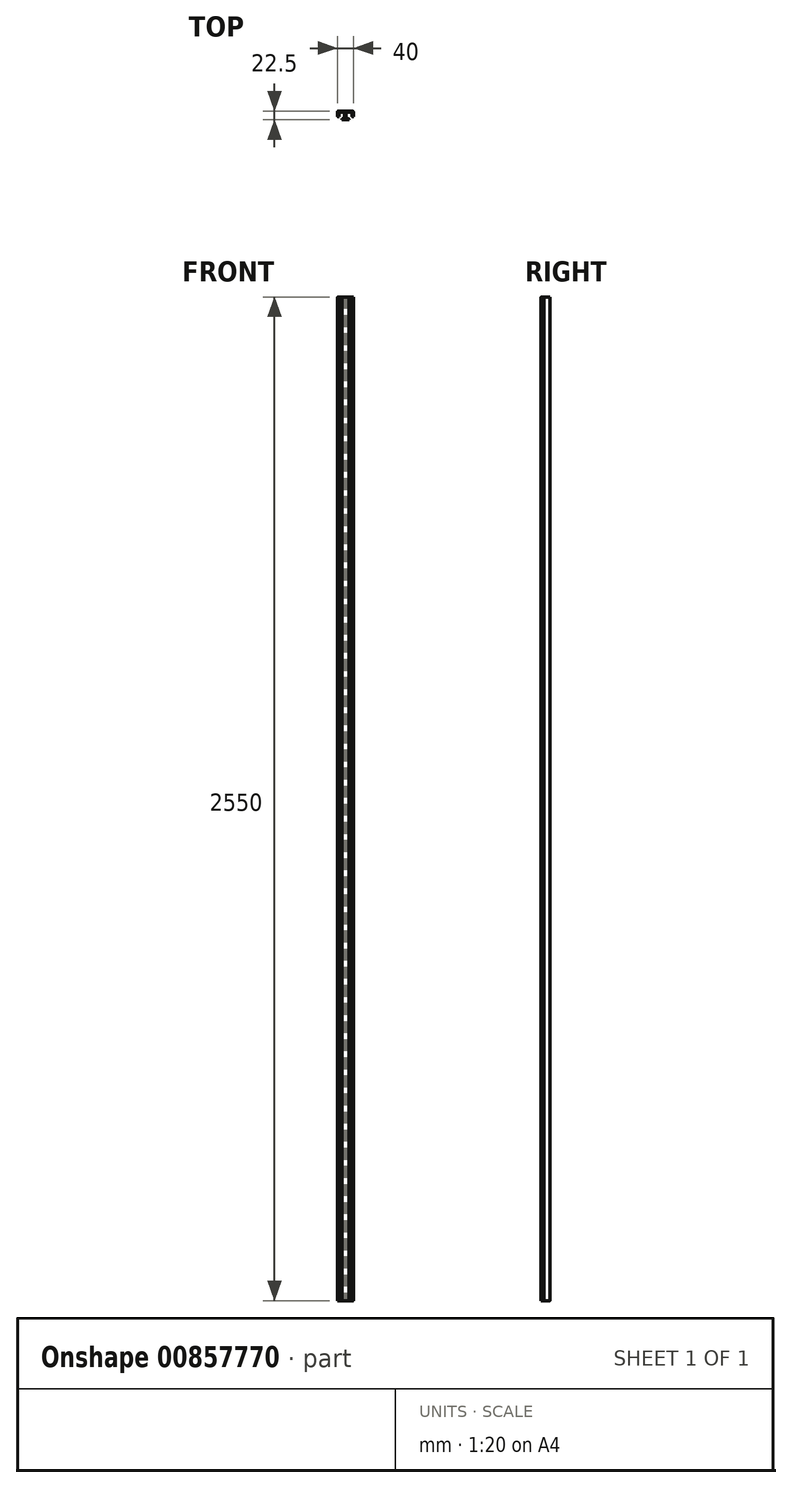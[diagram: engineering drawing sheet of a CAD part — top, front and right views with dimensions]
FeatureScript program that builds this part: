
annotation { "Feature Type Name" : "Feature", "Feature Type Description" : "" }
export const myFeature = defineFeature(function(context is Context, id is Id, definition is map)
    precondition{}
    {
        {
            var Q0;
            Q0=qCreatedBy(makeId("Top.planeOp"),FACE);
            var sketch = newSketch(context, id + "F0", { "sketchPlane" : qUnion([Q0])});
            skLineSegment(sketch, "E0", {"start": v(-20, 10) * mm, "end": v(20, 10) * mm});
            skLineSegment(sketch, "E1", {"start": v(20, 10) * mm, "end": v(20, -5) * mm});
            skLineSegment(sketch, "E2", {"start": v(-20, 10) * mm, "end": v(-20, -5) * mm});
            skLineSegment(sketch, "E3.0", {"start": v(-17, 7) * mm, "end": v(-17, -5) * mm});
            skLineSegment(sketch, "E3.1", {"start": v(-17, 7) * mm, "end": v(-2, 7) * mm});
            skLineSegment(sketch, "E3.2", {"start": v(17, 7) * mm, "end": v(17, -5) * mm});
            skLineSegment(sketch, "E4", {"start": v(-20, -5) * mm, "end": v(-17, -5) * mm});
            skLineSegment(sketch, "E5", {"start": v(17, -5) * mm, "end": v(20, -5) * mm});
            skLineSegment(sketch, "E6", {"start": v(-2, 7) * mm, "end": v(-2, -9.5) * mm});
            skLineSegment(sketch, "E7", {"start": v(-2, -9.5) * mm, "end": v(-8.5, -9.5) * mm});
            skLineSegment(sketch, "E8", {"start": v(-8.5, -9.5) * mm, "end": v(-8.5, -12.5) * mm});
            skLineSegment(sketch, "E9", {"start": v(-8.5, -12.5) * mm, "end": v(0, -12.5) * mm});
            skLineSegment(sketch, "E10.MirrorCS", {"start": v(2, 7) * mm, "end": v(2, -9.5) * mm});
            skLineSegment(sketch, "E11.MirrorCS", {"start": v(8.5, -12.5) * mm, "end": v(0, -12.5) * mm});
            skLineSegment(sketch, "E12.MirrorCS", {"start": v(2, -9.5) * mm, "end": v(8.5, -9.5) * mm});
            skLineSegment(sketch, "E13.MirrorCS", {"start": v(8.5, -9.5) * mm, "end": v(8.5, -12.5) * mm});
            skLineSegment(sketch, "E14.trimOffspring", {"start": v(2, 7) * mm, "end": v(17, 7) * mm});
            skSolve(sketch);
        }
        {
            var Q0;
            Q0=qSketchRegion(id+"F0",true);
            extrude(context, id + "F1", {"entities" : qUnion([Q0]), "depth" : 2550 * mm, "offsetDistance" : 25 * mm});
        }
        {
            var Q0;
            Q0=makeQuery(id+"F1.opExtrude","SWEPT_EDGE",EDGE,{"disambiguationData":[OSD([sQuery(id+"F0.wireOp",EDGE,"E0"),sQuery(id+"F0.wireOp",EDGE,"E2")])]});
            var Q1;
            Q1=makeQuery(id+"F1.opExtrude","SWEPT_EDGE",EDGE,{"disambiguationData":[OSD([sQuery(id+"F0.wireOp",EDGE,"E0"),sQuery(id+"F0.wireOp",EDGE,"E1")])]});
            fillet(context, id + "F2", {"entities" : qUnion([Q0, Q1]), "radius" : 2 * mm, "tangentPropagation" : true, "allowEdgeOverflow" : false});
        }
        {
            var Q0;
            Q0=makeQuery(id+"F1.opExtrude","SWEPT_EDGE",EDGE,{"disambiguationData":[OSD([sQuery(id+"F0.wireOp",EDGE,"E2"),sQuery(id+"F0.wireOp",EDGE,"E4")])]});
            var Q1;
            Q1=makeQuery(id+"F1.opExtrude","SWEPT_EDGE",EDGE,{"disambiguationData":[OSD([sQuery(id+"F0.wireOp",EDGE,"E3.0"),sQuery(id+"F0.wireOp",EDGE,"E4")])]});
            var Q2;
            Q2=makeQuery(id+"F1.opExtrude","SWEPT_EDGE",EDGE,{"disambiguationData":[OSD([sQuery(id+"F0.wireOp",EDGE,"E3.0"),sQuery(id+"F0.wireOp",EDGE,"E3.1")])]});
            var Q3;
            Q3=makeQuery(id+"F1.opExtrude","SWEPT_EDGE",EDGE,{"disambiguationData":[OSD([sQuery(id+"F0.wireOp",EDGE,"E10.MirrorCS"),sQuery(id+"F0.wireOp",EDGE,"E14.trimOffspring")])]});
            var Q4;
            Q4=makeQuery(id+"F1.opExtrude","SWEPT_EDGE",EDGE,{"disambiguationData":[OSD([sQuery(id+"F0.wireOp",EDGE,"E3.2"),sQuery(id+"F0.wireOp",EDGE,"E5")])]});
            var Q5;
            Q5=makeQuery(id+"F1.opExtrude","SWEPT_EDGE",EDGE,{"disambiguationData":[OSD([sQuery(id+"F0.wireOp",EDGE,"E1"),sQuery(id+"F0.wireOp",EDGE,"E5")])]});
            var Q6;
            Q6=makeQuery(id+"F1.opExtrude","SWEPT_EDGE",EDGE,{"disambiguationData":[OSD([sQuery(id+"F0.wireOp",EDGE,"E11.MirrorCS"),sQuery(id+"F0.wireOp",EDGE,"E13.MirrorCS")])]});
            var Q7;
            Q7=makeQuery(id+"F1.opExtrude","SWEPT_EDGE",EDGE,{"disambiguationData":[OSD([sQuery(id+"F0.wireOp",EDGE,"E12.MirrorCS"),sQuery(id+"F0.wireOp",EDGE,"E13.MirrorCS")])]});
            var Q8;
            Q8=makeQuery(id+"F1.opExtrude","SWEPT_EDGE",EDGE,{"disambiguationData":[OSD([sQuery(id+"F0.wireOp",EDGE,"E8"),sQuery(id+"F0.wireOp",EDGE,"E9")])]});
            var Q9;
            Q9=makeQuery(id+"F1.opExtrude","SWEPT_EDGE",EDGE,{"disambiguationData":[OSD([sQuery(id+"F0.wireOp",EDGE,"E7"),sQuery(id+"F0.wireOp",EDGE,"E8")])]});
            var Q10;
            Q10=makeQuery(id+"F1.opExtrude","SWEPT_EDGE",EDGE,{"disambiguationData":[OSD([sQuery(id+"F0.wireOp",EDGE,"E3.1"),sQuery(id+"F0.wireOp",EDGE,"E6")])]});
            var Q11;
            Q11=makeQuery(id+"F1.opExtrude","SWEPT_EDGE",EDGE,{"disambiguationData":[OSD([sQuery(id+"F0.wireOp",EDGE,"E3.2"),sQuery(id+"F0.wireOp",EDGE,"E14.trimOffspring")])]});
            var Q12;
            Q12=makeQuery(id+"F1.opExtrude","SWEPT_EDGE",EDGE,{"disambiguationData":[OSD([sQuery(id+"F0.wireOp",EDGE,"E10.MirrorCS"),sQuery(id+"F0.wireOp",EDGE,"E12.MirrorCS")])]});
            var Q13;
            Q13=makeQuery(id+"F1.opExtrude","SWEPT_EDGE",EDGE,{"disambiguationData":[OSD([sQuery(id+"F0.wireOp",EDGE,"E6"),sQuery(id+"F0.wireOp",EDGE,"E7")])]});
            fillet(context, id + "F3", {"entities" : qUnion([Q0, Q1, Q2, Q3, Q4, Q5, Q6, Q7, Q8, Q9, Q10, Q11, Q12, Q13]), "radius" : 1 * mm, "tangentPropagation" : true, "allowEdgeOverflow" : false});
        }
    });
